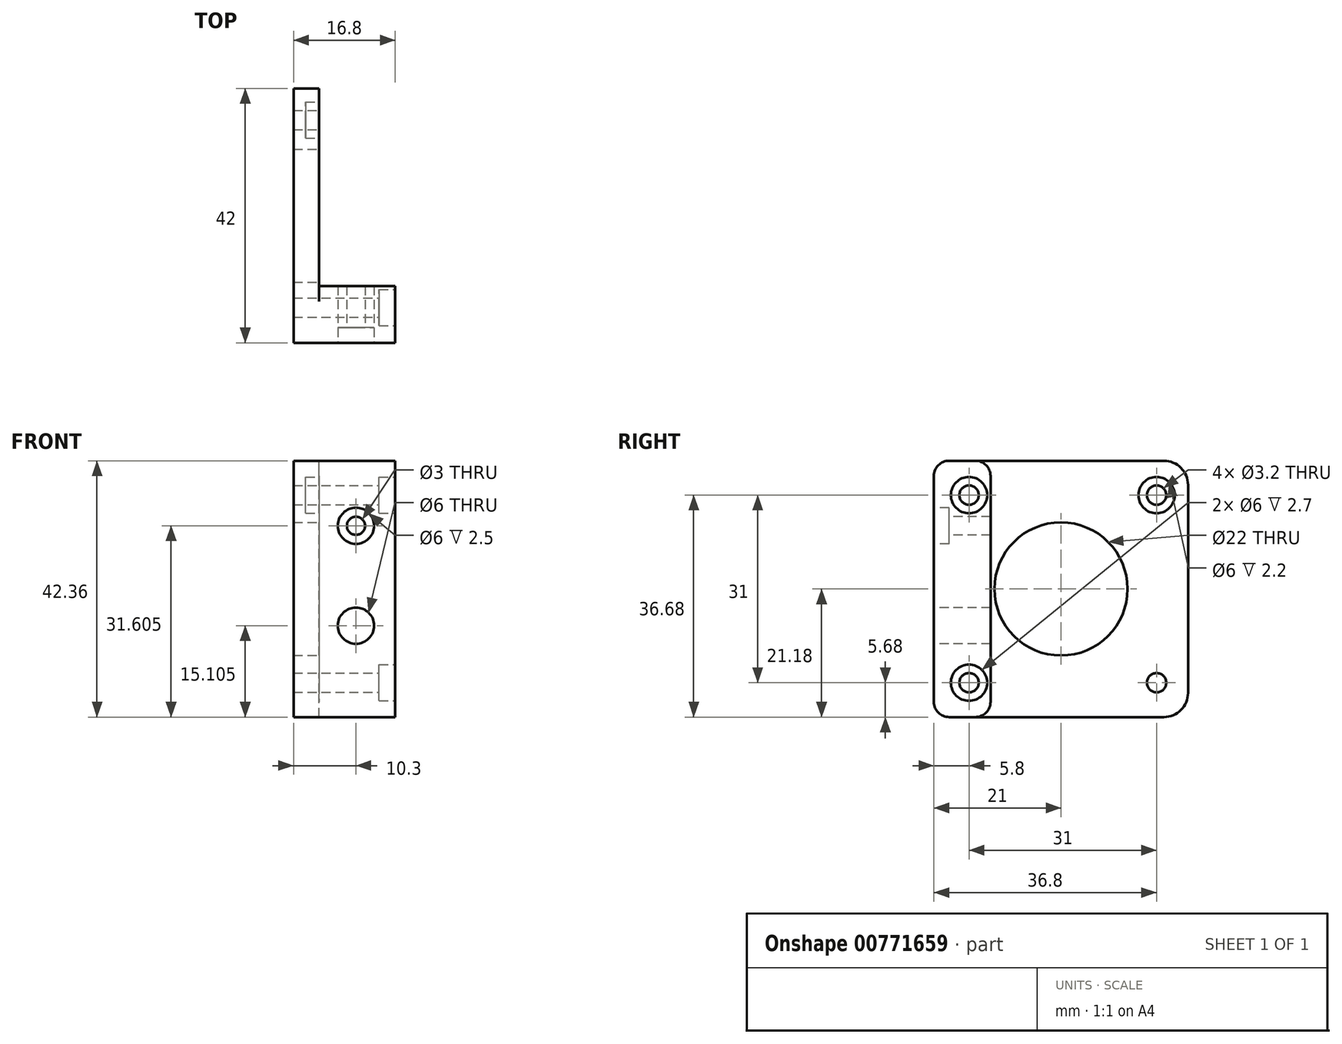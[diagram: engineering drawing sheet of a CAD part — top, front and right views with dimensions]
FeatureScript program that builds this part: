
annotation { "Feature Type Name" : "Feature", "Feature Type Description" : "" }
export const myFeature = defineFeature(function(context is Context, id is Id, definition is map)
    precondition{}
    {
        {
            var Q0;
            Q0=qCreatedBy(makeId("Right.planeOp"),FACE);
            var sketch = newSketch(context, id + "F0", { "sketchPlane" : qUnion([Q0])});
            skLineSegment(sketch, "E0.bottom", {"start": v(-21, 21.18) * mm, "end": v(21, 21.18) * mm});
            skLineSegment(sketch, "E0.top", {"start": v(-21, -21.18) * mm, "end": v(21, -21.18) * mm});
            skLineSegment(sketch, "E0.left", {"start": v(-21, 21.18) * mm, "end": v(-21, -21.18) * mm});
            skLineSegment(sketch, "E0.right", {"start": v(21, 21.18) * mm, "end": v(21, -21.18) * mm});
            skSolve(sketch);
        }
        {
            var Q0;
            Q0=makeQuery(id+"F0.imprint","IMPRINT",FACE,{"disambiguationData":[TD([[makeQuery(id+"F0.imprint","IMPRINT",EDGE,{"derivedFrom":sQuery(id+"F0.wireOp",EDGE,"E0.bottom")}),-1.0]])]});
            extrude(context, id + "F1", {"entities" : qUnion([Q0]), "depth" : 4.2 * mm, "offsetDistance" : 25 * mm});
        }
        {
            var Q0;
            Q0=makeQuery(id+"F1.opExtrude","CAP_FACE",FACE,{"disambiguationData":[OSD([sQuery(id+"F0.wireOp",EDGE,"E0.bottom"),sQuery(id+"F0.wireOp",EDGE,"E0.top"),sQuery(id+"F0.wireOp",EDGE,"E0.left"),sQuery(id+"F0.wireOp",EDGE,"E0.right")])],"isStart":false});
            var sketch = newSketch(context, id + "F2", { "sketchPlane" : qUnion([Q0])});
            skCircle(sketch, "E1", {"center": v(0, 0) * mm, "radius": 11 * mm});
            skCircle(sketch, "E2", {"center": v(15.8, 15.5) * mm, "radius": 1.6 * mm});
            skCircle(sketch, "E3", {"center": v(15.8, -15.5) * mm, "radius": 1.6 * mm});
            skSolve(sketch);
        }
        {
            var Q0;
            Q0 = qSketchRegion(id + "F2", true);
            extrude(context, id + "F3", {"entities" : qUnion([Q0]), "operationType" : NewBodyOperationType.REMOVE, "endBound" : BoundingType.THROUGH_ALL, "oppositeDirection" : true, "depth" : 25 * mm, "offsetDistance" : 25 * mm});
        }
        {
            var Q0;
            Q0=makeQuery(id+"F1.opExtrude","CAP_FACE",FACE,{"disambiguationData":[OSD([sQuery(id+"F0.wireOp",EDGE,"E0.bottom"),sQuery(id+"F0.wireOp",EDGE,"E0.top"),sQuery(id+"F0.wireOp",EDGE,"E0.left"),sQuery(id+"F0.wireOp",EDGE,"E0.right")])],"isStart":false});
            var sketch = newSketch(context, id + "F4", { "sketchPlane" : qUnion([Q0])});
            skLineSegment(sketch, "E4.bottom", {"start": v(-21, 21.18) * mm, "end": v(-11.65, 21.18) * mm});
            skLineSegment(sketch, "E4.top", {"start": v(-21, -21.18) * mm, "end": v(-11.65, -21.18) * mm});
            skLineSegment(sketch, "E4.left", {"start": v(-21, 21.18) * mm, "end": v(-21, -21.18) * mm});
            skLineSegment(sketch, "E4.right", {"start": v(-11.65, 21.18) * mm, "end": v(-11.65, -21.18) * mm});
            skSolve(sketch);
        }
        {
            var Q0;
            Q0 = qSketchRegion(id + "F4", true);
            extrude(context, id + "F5", {"entities" : qUnion([Q0]), "operationType" : NewBodyOperationType.ADD, "depth" : 12.6 * mm, "offsetDistance" : 25 * mm});
        }
        {
            var Q0;
            Q0=makeQuery(id+"F5.opExtrude","CAP_FACE",FACE,{"disambiguationData":[OSD([sQuery(id+"F4.wireOp",EDGE,"E4.bottom"),sQuery(id+"F4.wireOp",EDGE,"E4.top"),sQuery(id+"F4.wireOp",EDGE,"E4.left"),sQuery(id+"F4.wireOp",EDGE,"E4.right")])],"isStart":false});
            var sketch = newSketch(context, id + "F6", { "sketchPlane" : qUnion([Q0])});
            skCircle(sketch, "E5", {"center": v(-15.2, 15.5) * mm, "radius": 1.6 * mm});
            skCircle(sketch, "E6", {"center": v(-15.2, -15.5) * mm, "radius": 1.6 * mm});
            skSolve(sketch);
        }
        {
            var Q0;
            Q0 = qSketchRegion(id + "F6", true);
            extrude(context, id + "F7", {"entities" : qUnion([Q0]), "operationType" : NewBodyOperationType.REMOVE, "endBound" : BoundingType.THROUGH_ALL, "oppositeDirection" : true, "depth" : 25 * mm, "offsetDistance" : 25 * mm});
        }
        {
            var Q0;
            Q0=makeQuery(id+"F5.opExtrude","CAP_FACE",FACE,{"disambiguationData":[OSD([sQuery(id+"F4.wireOp",EDGE,"E4.bottom"),sQuery(id+"F4.wireOp",EDGE,"E4.top"),sQuery(id+"F4.wireOp",EDGE,"E4.left"),sQuery(id+"F4.wireOp",EDGE,"E4.right")])],"isStart":false});
            var sketch = newSketch(context, id + "F8", { "sketchPlane" : qUnion([Q0])});
            skCircle(sketch, "E7", {"center": v(-15.2, -15.5) * mm, "radius": 3 * mm});
            skCircle(sketch, "E8", {"center": v(-15.2, 15.5) * mm, "radius": 3 * mm});
            skSolve(sketch);
        }
        {
            var Q0;
            Q0 = qSketchRegion(id + "F8", true);
            extrude(context, id + "F9", {"entities" : qUnion([Q0]), "operationType" : NewBodyOperationType.REMOVE, "oppositeDirection" : true, "depth" : 2.7 * mm, "offsetDistance" : 25 * mm});
        }
        {
            var Q0;
            Q0=makeQuery(id+"F1.opExtrude","CAP_FACE",FACE,{"disambiguationData":[OSD([sQuery(id+"F0.wireOp",EDGE,"E0.bottom"),sQuery(id+"F0.wireOp",EDGE,"E0.top"),sQuery(id+"F0.wireOp",EDGE,"E0.left"),sQuery(id+"F0.wireOp",EDGE,"E0.right")])],"isStart":false});
            var sketch = newSketch(context, id + "F10", { "sketchPlane" : qUnion([Q0])});
            skCircle(sketch, "E9", {"center": v(15.8, 15.5) * mm, "radius": 3 * mm});
            skSolve(sketch);
        }
        {
            var Q0;
            Q0 = qSketchRegion(id + "F10", true);
            extrude(context, id + "F11", {"entities" : qUnion([Q0]), "operationType" : NewBodyOperationType.REMOVE, "oppositeDirection" : true, "depth" : 2.2 * mm, "offsetDistance" : 25 * mm});
        }
        {
            var Q0;
            Q0=makeQuery(id+"F1.opExtrude","SWEPT_EDGE",EDGE,{"disambiguationData":[OSD([sQuery(id+"F0.wireOp",EDGE,"E0.bottom"),sQuery(id+"F0.wireOp",EDGE,"E0.right")])]});
            var Q1;
            Q1=makeQuery(id+"F1.opExtrude","SWEPT_EDGE",EDGE,{"disambiguationData":[OSD([sQuery(id+"F0.wireOp",EDGE,"E0.top"),sQuery(id+"F0.wireOp",EDGE,"E0.right")])]});
            fillet(context, id + "F12", {"entities" : qUnion([Q0, Q1]), "radius" : 4 * mm, "tangentPropagation" : true, "allowEdgeOverflow" : false});
        }
        {
            var Q0;
            Q0=makeQuery(id+"F5.opExtrude","SWEPT_EDGE",EDGE,{"disambiguationData":[OSD([sQuery(id+"F0.wireOp",EDGE,"E0.bottom"),sQuery(id+"F4.wireOp",EDGE,"E4.bottom"),sQuery(id+"F4.wireOp",EDGE,"E4.right")])]});
            var Q1;
            Q1=makeQuery(id+"F5.opExtrude","SWEPT_EDGE",EDGE,{"disambiguationData":[OSD([sQuery(id+"F0.wireOp",EDGE,"E0.top"),sQuery(id+"F4.wireOp",EDGE,"E4.top"),sQuery(id+"F4.wireOp",EDGE,"E4.right")])]});
            var Q2;
            Q2=makeQuery(id+"F5.boolean.opBoolean","MERGE",EDGE,{"derivedFrom":[makeQuery(id+"F1.opExtrude","SWEPT_EDGE",EDGE,{"disambiguationData":[OSD([sQuery(id+"F0.wireOp",EDGE,"E0.bottom"),sQuery(id+"F0.wireOp",EDGE,"E0.left")])]}),makeQuery(id+"F5.opExtrude","SWEPT_EDGE",EDGE,{"disambiguationData":[OSD([sQuery(id+"F4.wireOp",EDGE,"E4.bottom"),sQuery(id+"F4.wireOp",EDGE,"E4.left")])]})]});
            var Q3;
            Q3=makeQuery(id+"F5.boolean.opBoolean","MERGE",EDGE,{"derivedFrom":[makeQuery(id+"F1.opExtrude","SWEPT_EDGE",EDGE,{"disambiguationData":[OSD([sQuery(id+"F0.wireOp",EDGE,"E0.top"),sQuery(id+"F0.wireOp",EDGE,"E0.left")])]}),makeQuery(id+"F5.opExtrude","SWEPT_EDGE",EDGE,{"disambiguationData":[OSD([sQuery(id+"F4.wireOp",EDGE,"E4.top"),sQuery(id+"F4.wireOp",EDGE,"E4.left")])]})]});
            fillet(context, id + "F13", {"entities" : qUnion([Q0, Q1, Q2, Q3]), "radius" : 2.5 * mm, "tangentPropagation" : true, "allowEdgeOverflow" : false});
        }
        {
            var Q0;
            Q0=makeQuery(id+"F5.boolean.opBoolean","MERGE",FACE,{"derivedFrom":[makeQuery(id+"F1.opExtrude","SWEPT_FACE",FACE,{"disambiguationData":[OSD([sQuery(id+"F0.wireOp",EDGE,"E0.left")])]}),makeQuery(id+"F5.opExtrude","SWEPT_FACE",FACE,{"disambiguationData":[OSD([sQuery(id+"F4.wireOp",EDGE,"E4.left")])]})]});
            var sketch = newSketch(context, id + "F14", { "sketchPlane" : qUnion([Q0])});
            skCircle(sketch, "E10", {"center": v(10.3, 10.43) * mm, "radius": 1.5 * mm});
            skCircle(sketch, "E11", {"center": v(10.3, -6.07) * mm, "radius": 3 * mm});
            skSolve(sketch);
        }
        {
            var Q0;
            Q0 = qSketchRegion(id + "F14", true);
            extrude(context, id + "F15", {"entities" : qUnion([Q0]), "operationType" : NewBodyOperationType.REMOVE, "endBound" : BoundingType.THROUGH_ALL, "oppositeDirection" : true, "depth" : 25 * mm, "offsetDistance" : 25 * mm});
        }
        {
            var Q0;
            Q0=makeQuery(id+"F5.boolean.opBoolean","MERGE",FACE,{"derivedFrom":[makeQuery(id+"F1.opExtrude","SWEPT_FACE",FACE,{"disambiguationData":[OSD([sQuery(id+"F0.wireOp",EDGE,"E0.left")])]}),makeQuery(id+"F5.opExtrude","SWEPT_FACE",FACE,{"disambiguationData":[OSD([sQuery(id+"F4.wireOp",EDGE,"E4.left")])]})]});
            var sketch = newSketch(context, id + "F16", { "sketchPlane" : qUnion([Q0])});
            skCircle(sketch, "E12", {"center": v(10.3, 10.43) * mm, "radius": 3 * mm});
            skSolve(sketch);
        }
        {
            var Q0;
            Q0 = qSketchRegion(id + "F16", true);
            extrude(context, id + "F17", {"entities" : qUnion([Q0]), "operationType" : NewBodyOperationType.REMOVE, "oppositeDirection" : true, "depth" : 2.5 * mm, "offsetDistance" : 25 * mm});
        }
    });
